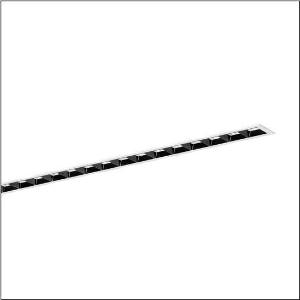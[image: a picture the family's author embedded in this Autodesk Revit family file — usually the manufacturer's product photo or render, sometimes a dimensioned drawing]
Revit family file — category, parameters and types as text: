
# Revit family: silica_21_51mx12da44wb
name_source: partatom
category: Lighting Fixtures
units: mm (PartAtom-declared; Revit-internal decimal feet)

## family parameters
Cut with Voids When Loaded = No
Host = Face
Light Source = No
Part Type = Normal
Room Calculation Point = No
Round Connector Dimension = Use Diameter
Shared = No

## types (1)
- --- (1 x LED, 4320 lm, 25.6 W, 4000K)
    Apparent Load = 26 VA
    CIE Flux Codes = 86 100 100 100 100
    Color Rendering = 80
    Color Temperature = 4000K
    Default Elevation = 1800 mm
    Description = Silica 21, office luminaire, primary light control with darklight reflector, of PMMA, black, CAT 2 (L<= 3000cd/m²), light emission: direct distribution, primary light characteristic: symmetric, installation type: recessed, LED, rated luminous flux: 4.320lm, luminous efficacy: 169lm/W, light colour: 840, colour temperature: 4000K, control gear: DALI 2, with terminal, 3+2-pole, max. 2.5mm², mains connection: 220..240V, AC, 50/60Hz, rated input power: 25.6W, luminaire housing, of aluminium, traffic white (RAL 9016), length: 1.228mm, width: 79mm, height: 53mm, protection rating (complete): IP20, insulation class (complete): insulation class I (protective earthing), certification: CE, ENEC, VDE, permissible operating ambient temperature: 0..+35°C, standard: EN 50419, packaging unit: 1 piece
    Height = 0 mm  [stored 0 ft]
    Lamp = 1 x LED
    Lamp Light Flux = 4320 lm
    Lamp Power = 25.6 W
    Lamp count = 1
    Length = 1227 mm
    Luminous efficacy = 169 lm/W
    Manufacturer = Siteco
    ModVariant = No
    Model = 51MX12DA44WB
    Mounting Place = Ceiling
    Mounting Type = Recessed
    Number of Poles = 1
    OnlyDefault = Yes
    Power Factor = 1
    Product Name = Silica 21
    Product group = office luminaire | ceiling recessed
    ProductGroupID = 400
    Protection Class = Protection class I
    Protection Degree = IP 20
    RLX_Detail_Level = 1
    RLX_Emergency_Light_Flux = 0 lm
    RLX_Emergency_Type = 0
    RLX_Emergency_Type_DB = No
    RlxData = <blob elided: 38629 chars, md5=958e6e3e>
    Socket = socket
    Standby Power = 0 W
    System Light Flux = 4320 lm
    System Power = 26 W
    Type Comments = factory setting: luminous flux: 100 % | dim-lin: 254 | 367 mA
    Type Image = l_1335880.jpg
    URL = http://relux.com
    VarID = @adj_030437
    Voltage = 0 V
    Weight = 0.00 kg
    Width = 79 mm

note: [stored X ft] marks values corroborated as IEEE doubles in the binary element streams (Revit-internal decimal feet)

## geometry (parser evidence)
native form markers: Blend x4, Sweep x11
no freeform markers — native parametric forms only
